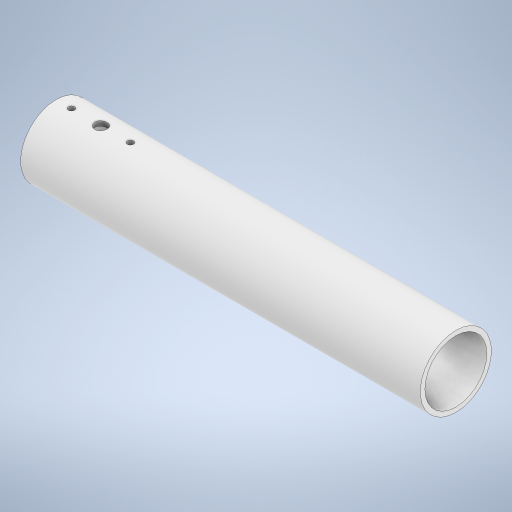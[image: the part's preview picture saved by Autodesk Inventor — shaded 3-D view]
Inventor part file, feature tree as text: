
AUTODESK INVENTOR PART (.ipt)
format: ipt  version: 2023 (Build 270158030, 158C)  size: 264,192 bytes
history: native  units: in
note: dims shown in document units (in); Inventor stores cm internally (conversion verified against a paired STEP export)
features: extrude x3, sketch x3
ambient origin geometry x8: Origin, YZ Plane, XZ Plane, XY Plane, X Axis, Y Axis, Z Axis, Center Point
bodies: Solid1 (feature_tree)
feature tree (6):
  extrude  "Extrusion1"  Depth=0.154in
  extrude  "Extrusion2"  Depth=0.4134in
  extrude  "Extrusion3"  TaperAngle=0.0deg  [1 undecoded]
  sketch  "Sketch1"  dims[d0=2.067in d1=0.154in]
  sketch  "Sketch2"  dims[d2=13.3465in d3=0.0in d4=0.4134in]
  sketch  "Sketch3"  dims[d5=1.5in d6=0.0in d7=0.0in d8=0.2067in d9=1.9685in d10=1.4961in d11=0.0in d12=0.0in]
note: 1 required parameter value undecoded (feature->parameter linkage not recoverable at this tier; creation-order binding heuristic only, values carry confidence <= 0.55)
